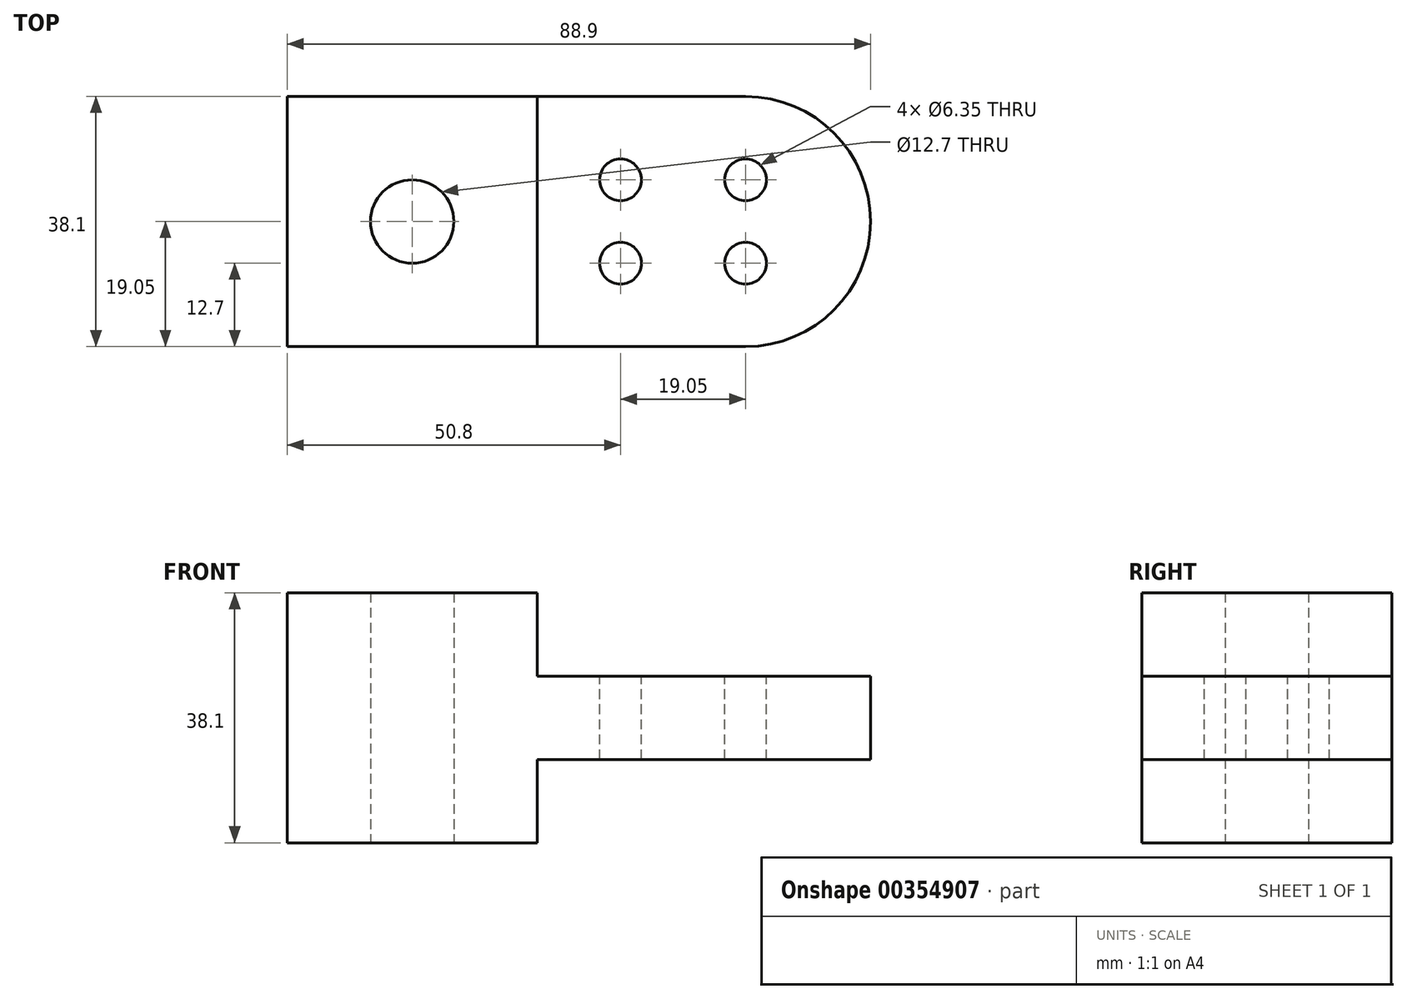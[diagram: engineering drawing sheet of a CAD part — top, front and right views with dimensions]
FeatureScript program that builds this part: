
annotation { "Feature Type Name" : "Feature", "Feature Type Description" : "" }
export const myFeature = defineFeature(function(context is Context, id is Id, definition is map)
    precondition{}
    {
        {
            var Q0;
            Q0=qCreatedBy(makeId("Top.planeOp"),FACE);
            var sketch = newSketch(context, id + "F0", { "sketchPlane" : qUnion([Q0])});
            skLineSegment(sketch, "E0.bottom", {"start": v(0, 0) * mm, "end": v(38.1, 0) * mm});
            skLineSegment(sketch, "E0.top", {"start": v(0, 38.1) * mm, "end": v(38.1, 38.1) * mm});
            skLineSegment(sketch, "E0.left", {"start": v(0, 0) * mm, "end": v(0, 38.1) * mm});
            skLineSegment(sketch, "E0.right", {"start": v(38.1, 0) * mm, "end": v(38.1, 38.1) * mm});
            skLineSegment(sketch, "E1", {"start": v(0, 0) * mm, "end": v(0, 19.05) * mm, "construction": true});
            skLineSegment(sketch, "E2", {"start": v(0, 19.05) * mm, "end": v(19.05, 19.05) * mm, "construction": true});
            skCircle(sketch, "E3", {"center": v(19.05, 19.05) * mm, "radius": 6.35 * mm});
            skSolve(sketch);
        }
        {
            var Q0;
            Q0=makeQuery(id+"F0.imprint","IMPRINT",FACE,{"disambiguationData":[TD([[makeQuery(id+"F0.imprint","IMPRINT",EDGE,{"derivedFrom":sQuery(id+"F0.wireOp",EDGE,"E0.bottom")}),1.0]])]});
            extrude(context, id + "F1", {"entities" : qUnion([Q0]), "depth" : 38.1 * mm});
        }
        {
            var Q0;
            Q0=makeQuery(id+"F1.opExtrude","CAP_FACE",FACE,{"disambiguationData":[OSD([sQuery(id+"F0.wireOp",EDGE,"E0.bottom"),sQuery(id+"F0.wireOp",EDGE,"E0.top"),sQuery(id+"F0.wireOp",EDGE,"E0.left"),sQuery(id+"F0.wireOp",EDGE,"E0.right"),sQuery(id+"F0.wireOp",EDGE,"E3")])],"isStart":false});
            var sketch = newSketch(context, id + "F2", { "sketchPlane" : qUnion([Q0])});
            skLineSegment(sketch, "E4", {"start": v(38.1, 38.1) * mm, "end": v(69.85, 38.1) * mm});
            skLineSegment(sketch, "E5", {"start": v(69.85, 38.1) * mm, "end": v(69.85, 0) * mm});
            skLineSegment(sketch, "E6", {"start": v(69.85, 0) * mm, "end": v(38.1, 0) * mm});
            skLineSegment(sketch, "E7", {"start": v(38.1, 0) * mm, "end": v(38.1, 38.1) * mm});
            skArc(sketch, "E8", {"start": v(69.85, 0) * mm, "mid": v(88.9, 19.05) * mm, "end": v(69.85, 38.1) * mm});
            skCircle(sketch, "E9", {"center": v(50.8, 25.4) * mm, "radius": 3.18 * mm});
            skCircle(sketch, "E10", {"center": v(69.85, 25.4) * mm, "radius": 3.18 * mm});
            skCircle(sketch, "E11", {"center": v(69.85, 12.7) * mm, "radius": 3.18 * mm});
            skCircle(sketch, "E12", {"center": v(50.8, 12.7) * mm, "radius": 3.18 * mm});
            skSolve(sketch);
        }
        {
            var Q0;
            {var subQ6=sQuery(id+"F2.wireOp",EDGE,"E4");Q0=makeQuery(id+"F2.imprint","IMPRINT",FACE,{"disambiguationData":[TD([[makeQuery(id+"F2.imprint","IMPRINT",EDGE,{"derivedFrom":subQ6}),-1.0]])]});}
            var Q1;
            {var subQ0=sQuery(id+"F2.wireOp",EDGE,"E8");Q1=makeQuery(id+"F2.imprint","IMPRINT",FACE,{"disambiguationData":[TD([[makeQuery(id+"F2.imprint","IMPRINT",EDGE,{"derivedFrom":subQ0}),1.0]])]});}
            extrude(context, id + "F3", {"entities" : qUnion([Q0, Q1]), "operationType" : NewBodyOperationType.ADD, "oppositeDirection" : true, "depth" : 25.4 * mm, "hasSecondDirection" : true, "secondDirectionOppositeDirection" : true, "secondDirectionDepth" : 12.7 * mm});
        }
    });
